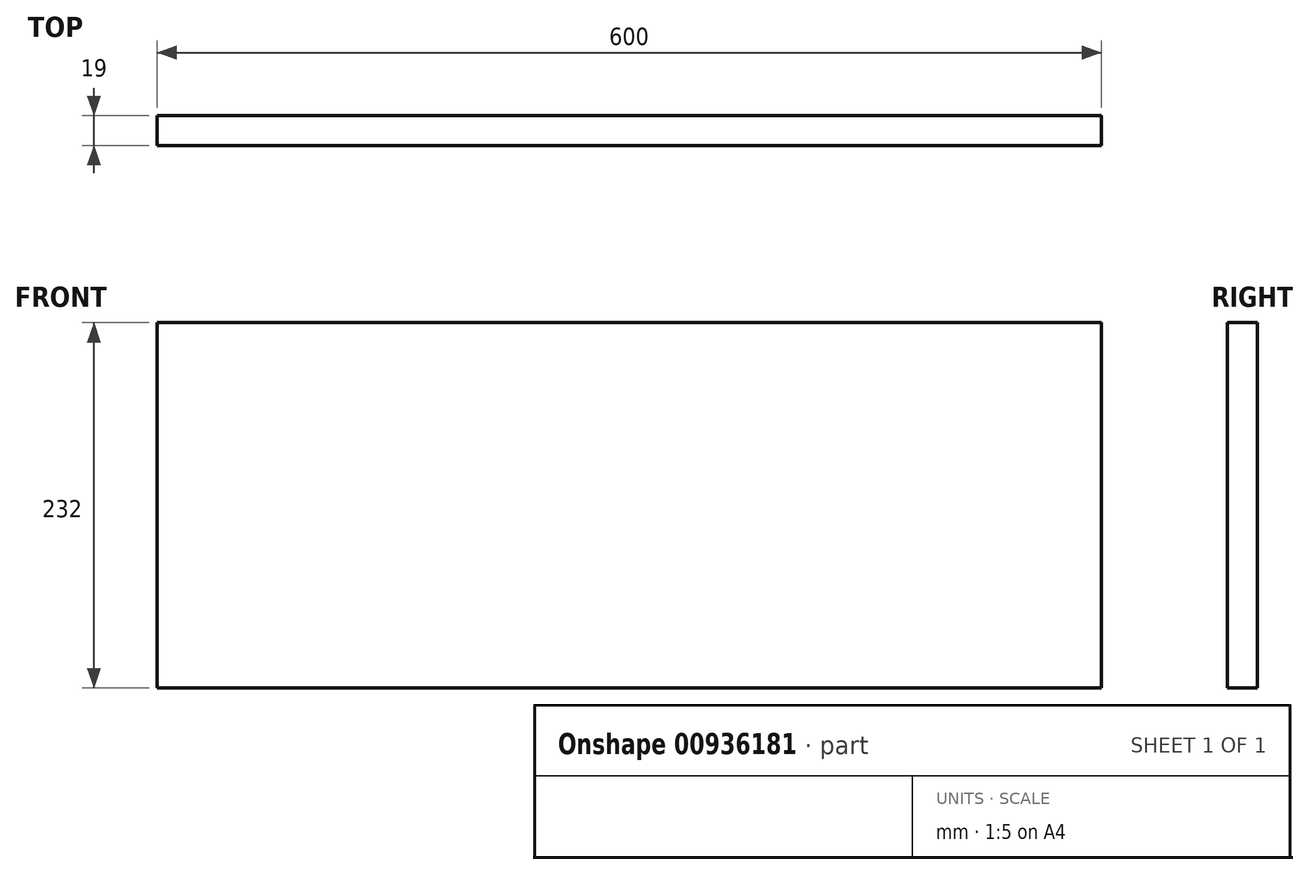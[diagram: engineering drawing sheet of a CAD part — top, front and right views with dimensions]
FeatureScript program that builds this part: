
annotation { "Feature Type Name" : "Feature", "Feature Type Description" : "" }
export const myFeature = defineFeature(function(context is Context, id is Id, definition is map)
    precondition{}
    {
        {
            var Q0;
            Q0=qCreatedBy(makeId("Front.planeOp"),FACE);
            var sketch = newSketch(context, id + "F0", { "sketchPlane" : qUnion([Q0])});
            skLineSegment(sketch, "E0.bottom", {"start": v(0, 0) * mm, "end": v(600, 0) * mm});
            skLineSegment(sketch, "E0.top", {"start": v(0, 232) * mm, "end": v(600, 232) * mm});
            skLineSegment(sketch, "E0.left", {"start": v(0, 0) * mm, "end": v(0, 232) * mm});
            skLineSegment(sketch, "E0.right", {"start": v(600, 0) * mm, "end": v(600, 232) * mm});
            skSolve(sketch);
        }
        {
            var Q0;
            Q0=makeQuery(id+"F0.imprint","IMPRINT",FACE,{"disambiguationData":[TD([[makeQuery(id+"F0.imprint","IMPRINT",EDGE,{"derivedFrom":sQuery(id+"F0.wireOp",EDGE,"E0.bottom")}),1.0]])]});
            extrude(context, id + "F1", {"entities" : qUnion([Q0]), "depth" : 19 * mm, "offsetDistance" : 25 * mm});
        }
    });
